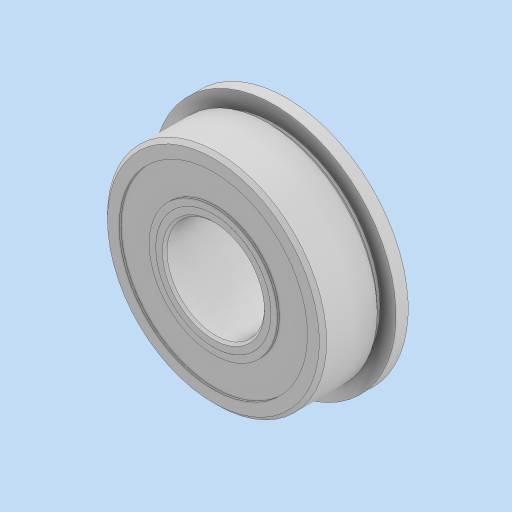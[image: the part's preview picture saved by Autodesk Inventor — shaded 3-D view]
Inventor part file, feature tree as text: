
AUTODESK INVENTOR PART (.ipt)
format: ipt  version: 2024 (Build 280153000, 153)  size: 654,336 bytes
history: native  units: in
note: dims shown in document units (in); Inventor stores cm internally (conversion verified against a paired STEP export)
features: other x14, revolve x3
ambient origin geometry x8: Origin, YZ Plane, XZ Plane, XY Plane, X Axis, Y Axis, Z Axis, Center Point
bodies: Solid1 (feature_tree), Solid2 (feature_tree), Solid3 (feature_tree), Solid4 (feature_tree), Solid5 (feature_tree), Solid6 (feature_tree), Solid7 (feature_tree), Solid8 (feature_tree), Solid9 (feature_tree), Solid10 (feature_tree), Solid11 (feature_tree), Solid12 (feature_tree), Solid13 (feature_tree), Solid14 (feature_tree), Solid15 (feature_tree), Solid16 (feature_tree), Solid17 (feature_tree)
feature tree (17):
  revolve  "Revolve2"  [1 undecoded]
  revolve  "Revolve4"  [1 undecoded]
  other  "Cut-Revolve1"
  revolve  "Revolve6[1]"  [1 undecoded]
  other  "CirPattern1[1]"
  other  "CirPattern1[2]"
  other  "CirPattern1[3]"
  other  "CirPattern1[4]"
  other  "CirPattern1[5]"
  other  "CirPattern1[6]"
  other  "CirPattern1[7]"
  other  "CirPattern1[8]"
  other  "CirPattern1[9]"
  other  "CirPattern1[10]"
  other  "CirPattern1[11]"
  other  "Cut-Extrude1"
  other  "Cut-Extrude2"
note: 3 required parameter values undecoded (feature->parameter linkage not recoverable at this tier; creation-order binding heuristic only, values carry confidence <= 0.55)
